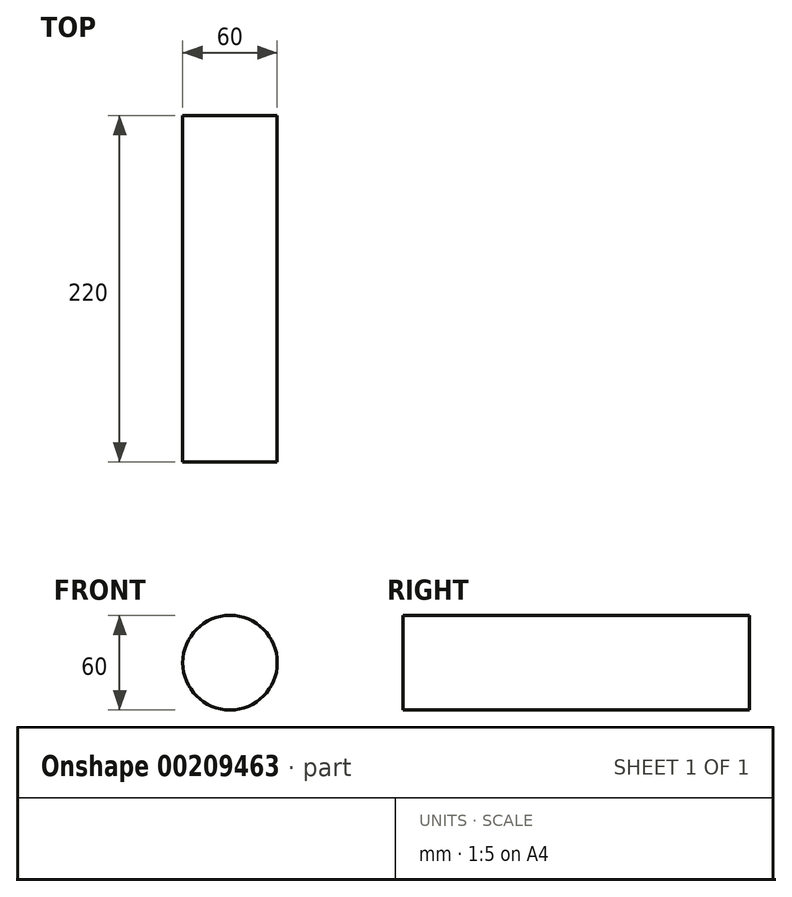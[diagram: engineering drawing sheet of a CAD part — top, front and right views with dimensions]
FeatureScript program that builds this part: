
annotation { "Feature Type Name" : "Feature", "Feature Type Description" : "" }
export const myFeature = defineFeature(function(context is Context, id is Id, definition is map)
    precondition{}
    {
        {
            var Q0;
            Q0=qCreatedBy(makeId("Front.planeOp"),FACE);
            var sketch = newSketch(context, id + "F0", { "sketchPlane" : qUnion([Q0])});
            skCircle(sketch, "E0", {"center": v(0, 0) * mm, "radius": 30 * mm});
            skSolve(sketch);
        }
        {
            var Q0;
            Q0=makeQuery(id+"F0.imprint","IMPRINT",FACE,{"disambiguationData":[TD([[makeQuery(id+"F0.imprint","IMPRINT",EDGE,{"derivedFrom":sQuery(id+"F0.wireOp",EDGE,"E0")}),1.0]])]});
            extrude(context, id + "F1", {"entities" : qUnion([Q0]), "depth" : 110 * mm, "hasSecondDirection" : true, "secondDirectionOppositeDirection" : true, "secondDirectionDepth" : 110 * mm});
        }
    });
